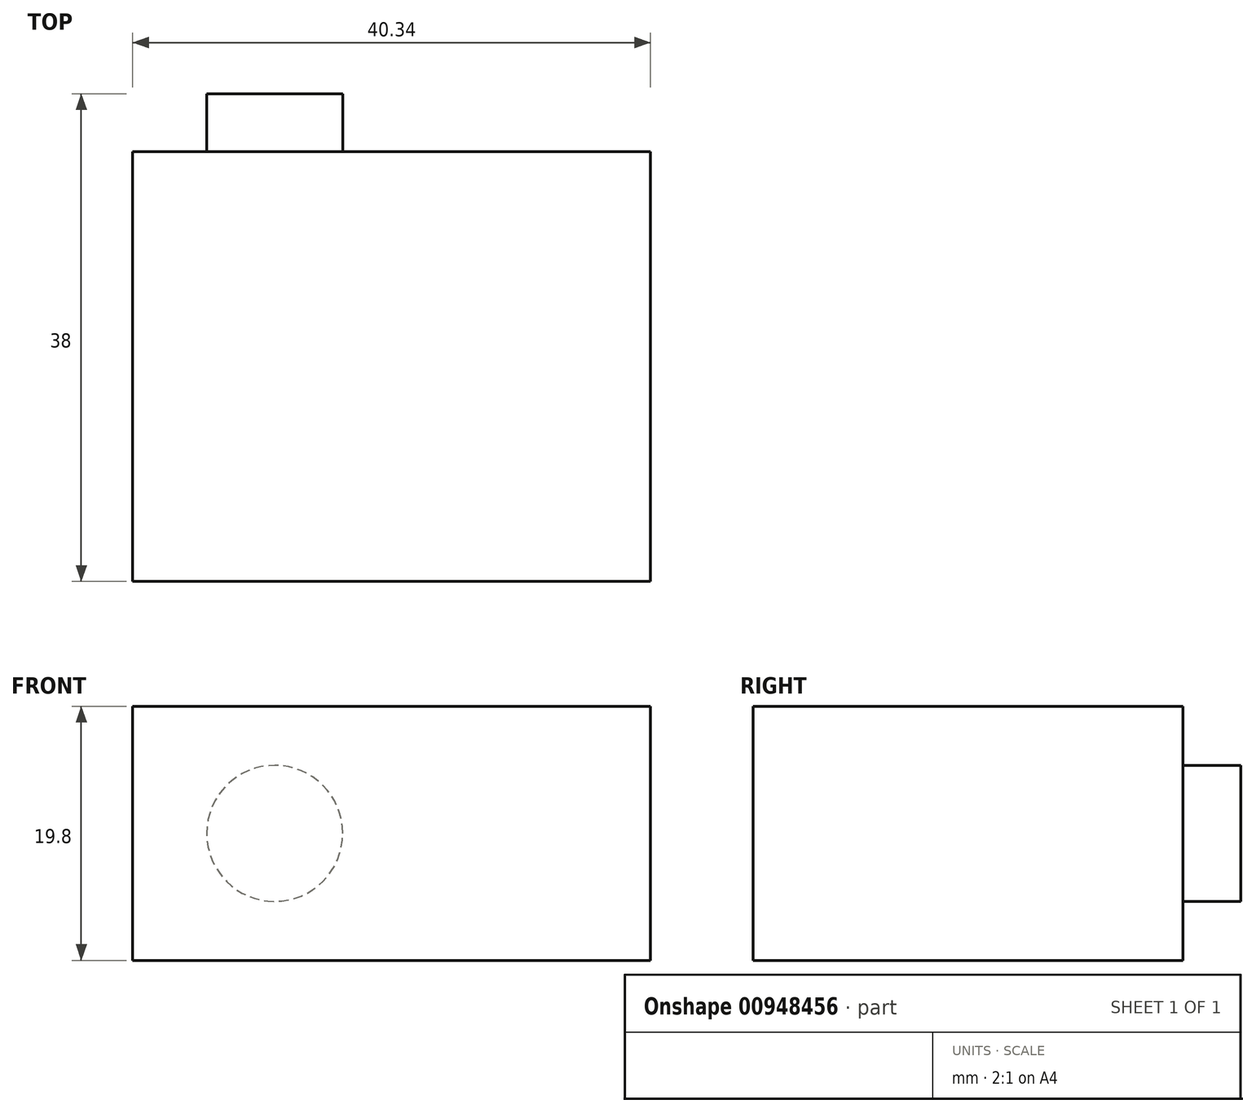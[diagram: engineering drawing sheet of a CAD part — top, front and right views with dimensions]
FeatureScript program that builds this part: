
annotation { "Feature Type Name" : "Feature", "Feature Type Description" : "" }
export const myFeature = defineFeature(function(context is Context, id is Id, definition is map)
    precondition{}
    {
        {
            var Q0;
            Q0=qCreatedBy(makeId("Front.planeOp"),FACE);
            var sketch = newSketch(context, id + "F0", { "sketchPlane" : qUnion([Q0])});
            skLineSegment(sketch, "E0.bottom", {"start": v(-20.18, 9.9) * mm, "end": v(20.18, 9.9) * mm});
            skLineSegment(sketch, "E0.top", {"start": v(-20.18, -9.9) * mm, "end": v(20.18, -9.9) * mm});
            skLineSegment(sketch, "E0.left", {"start": v(-20.18, 9.9) * mm, "end": v(-20.18, -9.9) * mm});
            skLineSegment(sketch, "E0.right", {"start": v(20.18, 9.9) * mm, "end": v(20.18, -9.9) * mm});
            skPoint(sketch, "E0.middle", {"position": v(0, 0) * mm});
            skSolve(sketch);
        }
        {
            var Q0;
            Q0=makeQuery(id+"F0.imprint","IMPRINT",FACE,{"disambiguationData":[TD([[makeQuery(id+"F0.imprint","IMPRINT",EDGE,{"derivedFrom":sQuery(id+"F0.wireOp",EDGE,"E0.bottom")}),-1.0]])]});
            extrude(context, id + "F1", {"entities" : qUnion([Q0]), "depth" : 33.5 * mm, "offsetDistance" : 25 * mm});
        }
        {
            var Q0;
            Q0=makeQuery(id+"F1.opExtrude","CAP_FACE",FACE,{"disambiguationData":[OSD([sQuery(id+"F0.wireOp",EDGE,"E0.bottom"),sQuery(id+"F0.wireOp",EDGE,"E0.top"),sQuery(id+"F0.wireOp",EDGE,"E0.left"),sQuery(id+"F0.wireOp",EDGE,"E0.right")])],"isStart":true});
            var sketch = newSketch(context, id + "F2", { "sketchPlane" : qUnion([Q0])});
            skCircle(sketch, "E1", {"center": v(9.1, 0) * mm, "radius": 5.3 * mm});
            skSolve(sketch);
        }
        {
            var Q0;
            Q0=makeQuery(id+"F2.imprint","IMPRINT",FACE,{"disambiguationData":[TD([[makeQuery(id+"F2.imprint","IMPRINT",EDGE,{"derivedFrom":sQuery(id+"F2.wireOp",EDGE,"E1")}),1.0]])]});
            extrude(context, id + "F3", {"entities" : qUnion([Q0]), "operationType" : NewBodyOperationType.ADD, "depth" : 4.5 * mm, "offsetDistance" : 25 * mm});
        }
    });
